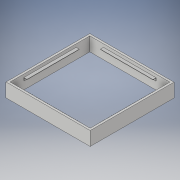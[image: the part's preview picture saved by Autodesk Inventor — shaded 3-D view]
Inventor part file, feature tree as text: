
AUTODESK INVENTOR PART (.ipt)
format: ipt  version: 2018 (Build 220112000, 112)  size: 189,952 bytes
history: native  units: in
note: dims shown in document units (in); Inventor stores cm internally (conversion verified against a paired STEP export)
features: extrude x9, sketch x9
ambient origin geometry x8: Origin, YZ Plane, XZ Plane, XY Plane, X Axis, Y Axis, Z Axis, Center Point
bodies: Body1 (feature_tree)
feature tree (18):
  extrude  "Extrusion12"  Depth=29.125in
  sketch  "Sketch16"  dims[d86=0.754in d87=0.754in]
  sketch  "Sketch17"  dims[d88=0.754in d89=0.754in]
  sketch  "Sketch18"  dims[d90=5.0in d91=0.0in d92=5.0in]
  extrude  "Extrusion13"  Depth=0.754in
  extrude  "Extrusion14"  Depth=0.754in
  extrude  "Extrusion15"  Depth=5.0in
  extrude  "Extrusion16"  Depth=2.9in
  extrude  "Extrusion17"  Depth=5.0in
  sketch  "Sketch21"  dims[d97=5.0in d98=1.0in]
  extrude  "Extrusion18"  Depth=1.0in
  extrude  "Extrusion19"  Depth=5.0in
  extrude  "Extrusion20"  Depth=1.0in
  sketch  "Sketch15"  dims[d84=29.0in d85=29.125in]
  sketch  "Sketch19"  dims[d93=5.0in d94=2.9in]
  sketch  "Sketch20"  dims[d95=1.0in d96=5.0in]
  sketch  "Sketch22"  dims[d99=2.9in d100=5.0in]
  sketch  "Sketch23"  dims[d101=5.0in d102=1.0in d103=2.9in d104=5.0in d105=5.0in d106=1.0in d107=2.9in d108=0.125in d109=0.0in d110=0.125in d111=0.0in d112=0.125in d113=0.0in d114=0.125in d115=0.0in d116=0.125in d117=1.0in d118=0.0in d119=0.125in d120=0.125in d121=1.0in d122=0.0in d123=1.0in d124=0.0in d125=0.125in d126=1.0in d127=0.0in]
